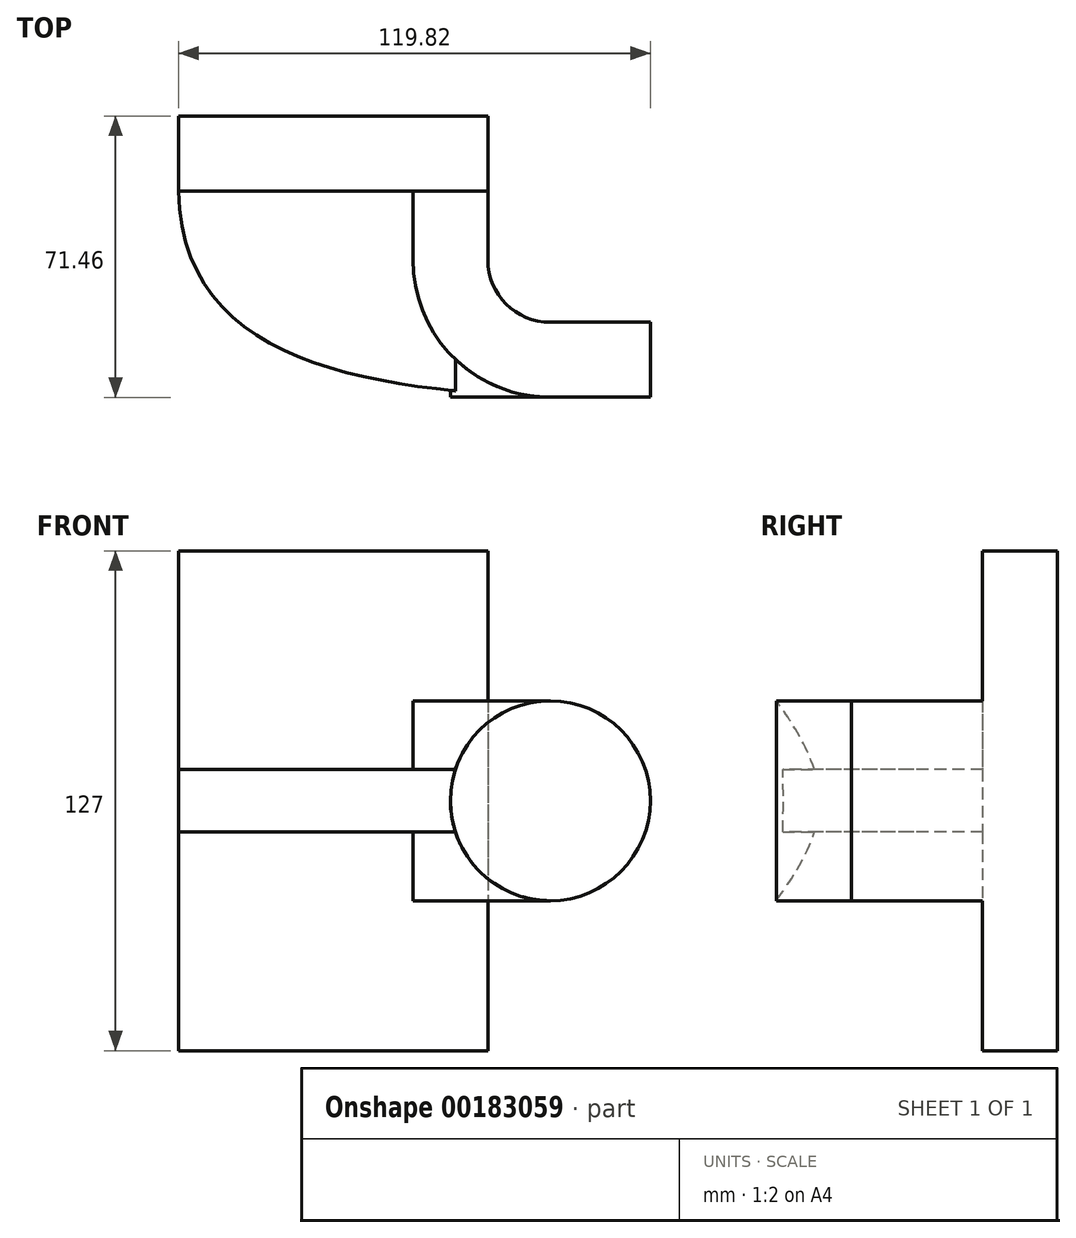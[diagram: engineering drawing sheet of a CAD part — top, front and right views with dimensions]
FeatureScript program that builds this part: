
annotation { "Feature Type Name" : "Feature", "Feature Type Description" : "" }
export const myFeature = defineFeature(function(context is Context, id is Id, definition is map)
    precondition{}
    {
        {
            var Q0;
            Q0=qCreatedBy(makeId("Top.planeOp"),FACE);
            var sketch = newSketch(context, id + "F0", { "sketchPlane" : qUnion([Q0])});
            skLineSegment(sketch, "E0.bottom", {"start": v(-39.27, 9.52) * mm, "end": v(39.27, 9.52) * mm});
            skLineSegment(sketch, "E0.top", {"start": v(-39.27, -9.52) * mm, "end": v(39.27, -9.52) * mm});
            skLineSegment(sketch, "E0.left", {"start": v(-39.27, 9.52) * mm, "end": v(-39.27, -9.52) * mm});
            skLineSegment(sketch, "E0.right", {"start": v(39.27, 9.52) * mm, "end": v(39.27, -9.52) * mm});
            skPoint(sketch, "E0.middle", {"position": v(0, 0) * mm});
            skLineSegment(sketch, "E1.bottom", {"start": v(55.15, -38.1) * mm, "end": v(105.95, -38.1) * mm});
            skLineSegment(sketch, "E1.top", {"start": v(55.15, -66.68) * mm, "end": v(105.95, -66.68) * mm});
            skLineSegment(sketch, "E1.left", {"start": v(55.15, -38.1) * mm, "end": v(55.15, -66.68) * mm});
            skLineSegment(sketch, "E1.right", {"start": v(105.95, -38.1) * mm, "end": v(105.95, -66.68) * mm});
            skPoint(sketch, "E1.middle", {"position": v(80.55, -52.39) * mm});
            skLineSegment(sketch, "E2", {"start": v(39.27, -9.52) * mm, "end": v(39.27, -27) * mm});
            skArc(sketch, "E3", {"start": v(39.27, -27) * mm, "mid": v(43.92, -38.23) * mm, "end": v(55.15, -42.88) * mm});
            skLineSegment(sketch, "E4", {"start": v(55.15, -42.88) * mm, "end": v(85.8, -42.88) * mm});
            skLineSegment(sketch, "E5.0", {"start": v(55.15, -61.93) * mm, "end": v(85.8, -61.93) * mm});
            skArc(sketch, "E5.1", {"start": v(20.22, -27) * mm, "mid": v(30.45, -51.7) * mm, "end": v(55.15, -61.93) * mm});
            skLineSegment(sketch, "E5.2", {"start": v(20.22, -9.53) * mm, "end": v(20.22, -27) * mm});
            skLineSegment(sketch, "E6", {"start": v(80.55, -38.1) * mm, "end": v(80.55, -66.68) * mm});
            skFitSpline(sketch, "E7", {"points": [v(-39.27, -9.52) * mm, v(55.15, -61.93) * mm], "startDerivative": vector(2.2, -132.18) * mm, "endDerivative": vector(138.8, -6.12) * mm});
            skSolve(sketch);
        }
        {
            var Q0;
            Q0=makeQuery(id+"F0.imprint","IMPRINT",FACE,{"disambiguationData":[TD([[makeQuery(id+"F0.imprint","IMPRINT",EDGE,{"derivedFrom":sQuery(id+"F0.wireOp",EDGE,"E0.bottom")}),-1.0]])]});
            extrude(context, id + "F1", {"entities" : qUnion([Q0]), "endBound" : BoundingType.SYMMETRIC, "depth" : 127 * mm});
        }
        {
            var Q0;
            {var subQ1=sQuery(id+"F0.wireOp",EDGE,"E2");Q0=makeQuery(id+"F0.imprint","IMPRINT",FACE,{"disambiguationData":[TD([[makeQuery(id+"F0.imprint","IMPRINT",EDGE,{"derivedFrom":subQ1}),-1.0]])]});}
            extrude(context, id + "F2", {"entities" : qUnion([Q0]), "operationType" : NewBodyOperationType.ADD, "endBound" : BoundingType.SYMMETRIC, "depth" : 50.8 * mm});
        }
        {
            var Q0;
            {var subQ3=sQuery(id+"F0.wireOp",EDGE,"E5.2");Q0=makeQuery(id+"F0.imprint","IMPRINT",FACE,{"disambiguationData":[TD([[makeQuery(id+"F0.imprint","IMPRINT",EDGE,{"derivedFrom":subQ3}),-1.0]])]});}
            extrude(context, id + "F3", {"entities" : qUnion([Q0]), "operationType" : NewBodyOperationType.ADD, "endBound" : BoundingType.SYMMETRIC, "depth" : 15.88 * mm});
        }
        {
            var Q0;
            {var subQ0=sQuery(id+"F0.wireOp",EDGE,"E4");var subQ5=sQuery(id+"F0.wireOp",EDGE,"E6");var subQ6=makeQuery(id+"F0.imprint","INTERSECT",VERTEX,{"derivedFrom":[subQ0,subQ5]});Q0=makeQuery(id+"F0.imprint","IMPRINT",FACE,{"disambiguationData":[TD([[makeQuery(id+"F0.imprint","IMPRINT",EDGE,{"disambiguationData":[TD([[subQ6,-1.0]])],"derivedFrom":subQ5}),-1.0]])]});}
            var Q1;
            Q1=sQuery(id+"F0.wireOp",EDGE,"E1.left");
            revolve(context, id + "F4", {"operationType" : NewBodyOperationType.ADD, "entities" : qUnion([Q0]), "axis" : qUnion([Q1]), "revolveType" : RevolveType.FULL});
        }
    });
